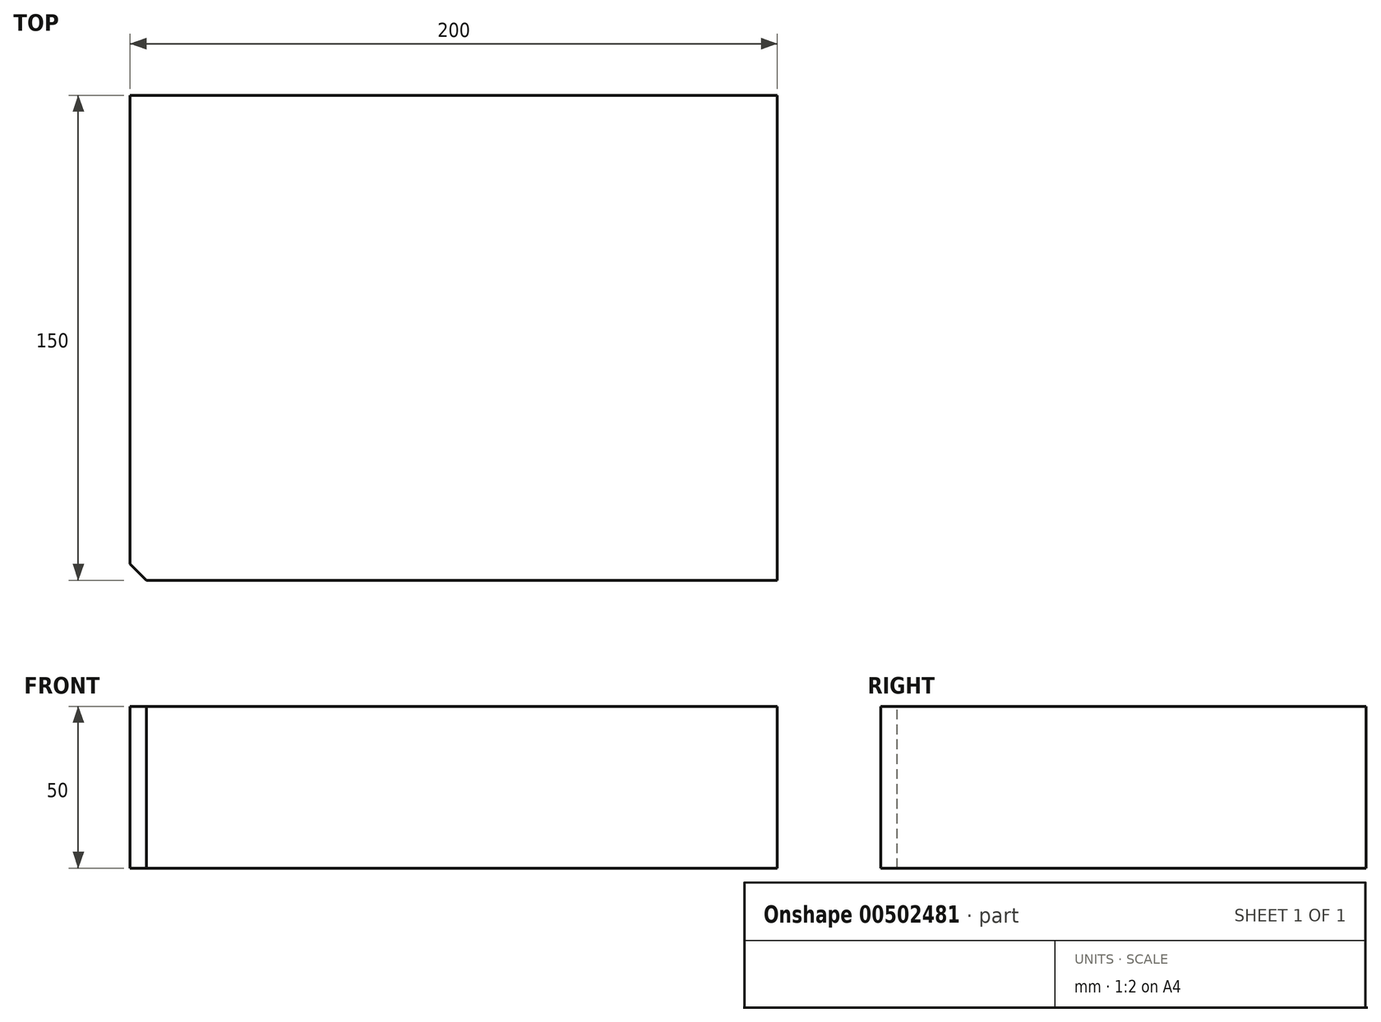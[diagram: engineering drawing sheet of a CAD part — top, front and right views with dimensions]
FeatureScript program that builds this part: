
annotation { "Feature Type Name" : "Feature", "Feature Type Description" : "" }
export const myFeature = defineFeature(function(context is Context, id is Id, definition is map)
    precondition{}
    {
        {
            var Q0;
            Q0=qCreatedBy(makeId("Top.planeOp"),FACE);
            var sketch = newSketch(context, id + "F0", { "sketchPlane" : qUnion([Q0])});
            skLineSegment(sketch, "E0.bottom", {"start": v(-100, -75) * mm, "end": v(100, -75) * mm});
            skLineSegment(sketch, "E0.top", {"start": v(-100, 75) * mm, "end": v(100, 75) * mm});
            skLineSegment(sketch, "E0.left", {"start": v(-100, -75) * mm, "end": v(-100, 75) * mm});
            skLineSegment(sketch, "E0.right", {"start": v(100, -75) * mm, "end": v(100, 75) * mm});
            skPoint(sketch, "E0.middle", {"position": v(0, 0) * mm});
            skSolve(sketch);
        }
        {
            var Q0;
            Q0 = qSketchRegion(id + "F0", true);
            extrude(context, id + "F1", {"entities" : qUnion([Q0]), "depth" : 50 * mm});
        }
        {
            var Q0;
            Q0=makeQuery(id+"F1.opExtrude","SWEPT_EDGE",EDGE,{"disambiguationData":[OSD([sQuery(id+"F0.wireOp",EDGE,"E0.bottom"),sQuery(id+"F0.wireOp",EDGE,"E0.left")])]});
            chamfer(context, id + "F2", {"entities" : qUnion([Q0]), "width" : 5 * mm, "tangentPropagation" : true});
        }
    });
